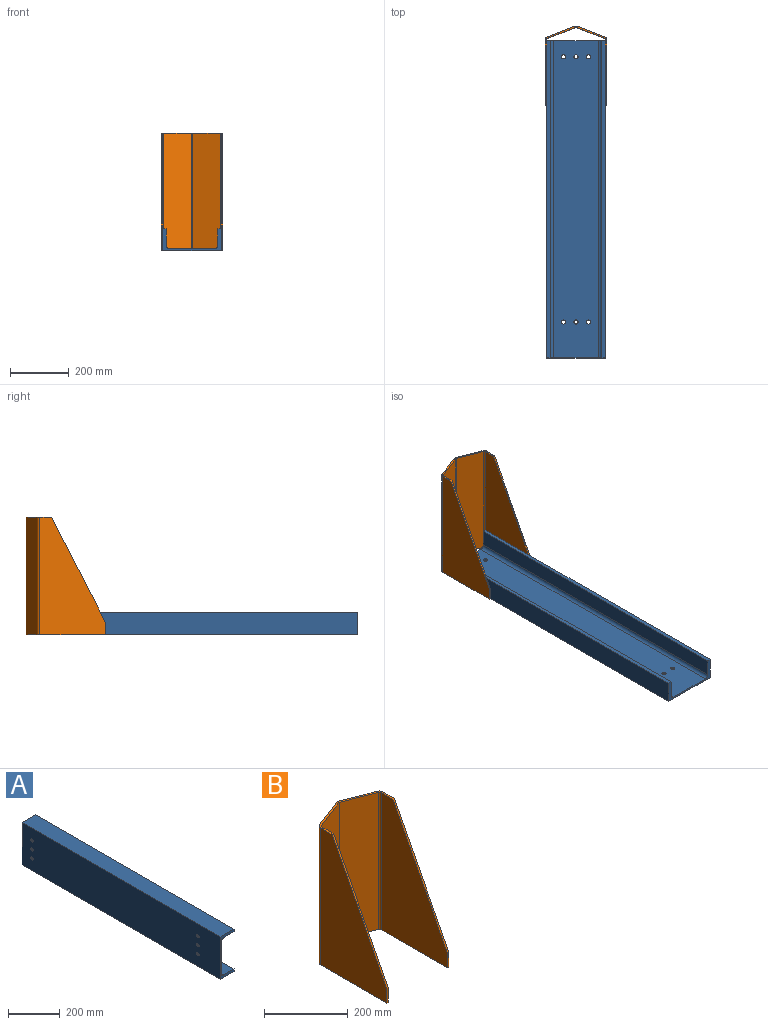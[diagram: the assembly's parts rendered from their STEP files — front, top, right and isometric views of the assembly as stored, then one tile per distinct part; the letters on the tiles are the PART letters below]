
ASSEMBLY  parts=2 mates=1
PART A: 18 faces, bbox 75x1080x200 mm
  f0: cylinder r=7mm len=14mm, axis (1,0,0), area 263.9mm2, adj f8,f13
  f1: cylinder r=7mm len=14mm, axis (1,0,0), area 263.9mm2, adj f8,f13
  f2: cylinder r=7mm len=14mm, axis (1,0,0), area 263.9mm2, adj f8,f13
  f3: cylinder r=7mm len=14mm, axis (1,0,0), area 263.9mm2, adj f8,f13
  f4: cylinder r=7mm len=14mm, axis (1,0,0), area 263.9mm2, adj f8,f13
  f5: cylinder r=7mm len=14mm, axis (1,0,0), area 263.9mm2, adj f8,f13
  f6: plane 200x75mm, normal (0,1,0), area 2917.8mm2, adj f7,f8,f9,f10,f11,f12,f13,f14
  f7: cylinder r=12mm len=1080mm, axis (0,1,0), area 20357.5mm2, adj f6,f8,f16,f17
  f8: plane 1080x152mm, normal (1,0,0), area 163236.4mm2, adj f0,f1,f2,f3,f4,f5,f6,f7
  f9: cylinder r=12mm len=1080mm, axis (0,1,0), area 20357.5mm2, adj f6,f8,f10,f17
  f10: plane 1080x57mm, normal (0,0,1), area 61560mm2, adj f6,f9,f11,f17
  f11: plane 1080x12mm, normal (1,0,0), area 12960mm2, adj f6,f10,f12,f17
  f12: plane 1080x75mm, normal (0,0,-1), area 81000mm2, adj f6,f11,f13,f17
  f13: plane 1080x200mm, normal (-1,0,0), area 215076.4mm2, adj f0,f1,f2,f3,f4,f5,f6,f12
  f14: plane 1080x75mm, normal (0,0,1), area 81000mm2, adj f6,f13,f15,f17
  f15: plane 1080x12mm, normal (1,0,0), area 12960mm2, adj f6,f14,f16,f17
  f16: plane 1080x57mm, normal (0,0,-1), area 61560mm2, adj f6,f7,f15,f17
  f17: plane 200x75mm, normal (0,-1,0), area 2917.8mm2, adj f7,f8,f9,f10,f11,f12,f13,f14
PART B: 20 faces, bbox 210x270.4x400 mm
  f0: plane 43x5mm, normal (0,-1,0), area 215mm2, adj f8,f9,f17,f19
  f1: plane 43x5mm, normal (0,-1,0), area 215mm2, adj f2,f15,f17,f18
  f2: plane 400x223.82mm, normal (1,0,0), area 56715.9mm2, adj f1,f3,f16,f17,f18
  f3: plane 210x86.54mm, normal (0,0,1), area 1535.7mm2, adj f2,f4,f5,f6,f7,f8,f9,f10
  f4: plane 400x95mm, normal (0.36,0.93,0), area 40713.8mm2, adj f3,f5,f16,f17
  f5: cylinder r=10mm len=400mm, axis (0,0,-1), area 2937.4mm2, adj f3,f4,f6,f17
  f6: plane 400x95mm, normal (-0.36,0.93,0), area 40713.8mm2, adj f3,f5,f7,f17
  f7: cylinder r=10mm len=400mm, axis (0,0,-1), area 4814.5mm2, adj f3,f6,f8,f17
  f8: plane 400x223.82mm, normal (-1,0,0), area 56715.9mm2, adj f0,f3,f7,f17,f19
  f9: plane 400x223.82mm, normal (1,0,0), area 56715.9mm2, adj f0,f3,f10,f17,f19
  f10: cylinder r=5mm len=400mm, axis (0,0,-1), area 2407.2mm2, adj f3,f9,f11,f17
  f11: plane 400x95mm, normal (0.36,-0.93,0), area 40713.8mm2, adj f3,f10,f12,f17
  f12: cylinder r=5mm len=400mm, axis (0,0,-1), area 1468.7mm2, adj f3,f11,f13,f17
  f13: plane 400x95mm, normal (-0.36,-0.93,0), area 40713.8mm2, adj f3,f12,f14,f17
  f14: cylinder r=5mm len=400mm, axis (0,0,-1), area 2407.2mm2, adj f3,f13,f15,f17
  f15: plane 400x223.82mm, normal (-1,0,0), area 56715.9mm2, adj f1,f3,f14,f17,f18
  f16: cylinder r=10mm len=400mm, axis (0,0,-1), area 4814.5mm2, adj f2,f3,f4,f17
  f17: plane 270.36x210mm, normal (0,0,-1), area 3373.8mm2, adj f0,f1,f2,f4,f5,f6,f7,f8
  f18: plane 357x183.82mm, normal (0,-0.89,0.46), area 2007.7mm2, adj f1,f2,f3,f15
  f19: plane 357x183.82mm, normal (0,-0.89,0.46), area 2007.7mm2, adj f0,f3,f8,f9
PLACE A rot(axis=(0,-1,0),90deg) t=(-408.9,901.92,29.32)mm
PLACE B t=(-632.4,653.24,29.32)mm
MATE fastened B.f9 <-> A.f14  axis (1,0,0) through (-608.9,681.22,29.32)mm
